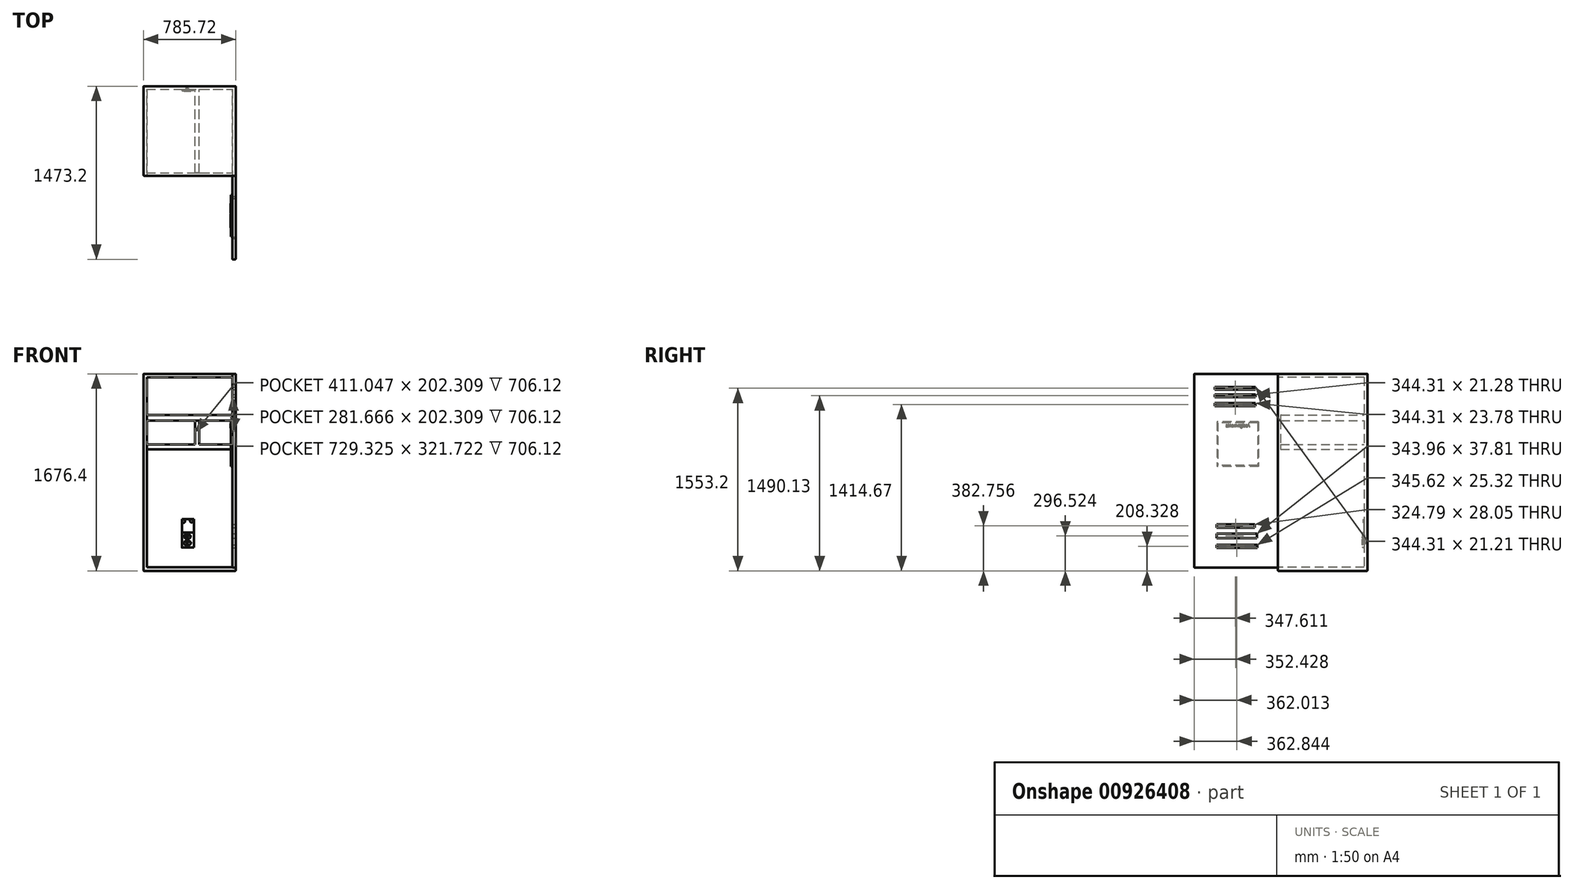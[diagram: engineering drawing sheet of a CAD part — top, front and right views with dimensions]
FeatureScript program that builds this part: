
annotation { "Feature Type Name" : "Feature", "Feature Type Description" : "" }
export const myFeature = defineFeature(function(context is Context, id is Id, definition is map)
    precondition{}
    {
        {
            var Q0;
            Q0=qCreatedBy(makeId("Top.planeOp"),FACE);
            var sketch = newSketch(context, id + "F0", { "sketchPlane" : qUnion([Q0])});
            skLineSegment(sketch, "E0.bottom", {"start": v(-392.86, 381) * mm, "end": v(392.86, 381) * mm});
            skLineSegment(sketch, "E0.top", {"start": v(-392.86, -381) * mm, "end": v(392.86, -381) * mm});
            skLineSegment(sketch, "E0.left", {"start": v(-392.86, 381) * mm, "end": v(-392.86, -381) * mm});
            skLineSegment(sketch, "E0.right", {"start": v(392.86, 381) * mm, "end": v(392.86, -381) * mm});
            skPoint(sketch, "E0.middle", {"position": v(0, 0) * mm});
            skSolve(sketch);
        }
        {
            var Q0;
            Q0=makeQuery(id+"F0.imprint","IMPRINT",FACE,{"disambiguationData":[TD([[makeQuery(id+"F0.imprint","IMPRINT",EDGE,{"derivedFrom":sQuery(id+"F0.wireOp",EDGE,"E0.bottom")}),-1.0]])]});
            extrude(context, id + "F1", {"entities" : qUnion([Q0]), "depth" : 1676.4 * mm, "offsetDistance" : 25.4 * mm});
        }
        {
            var Q0;
            Q0=makeQuery(id+"F1.opExtrude","SWEPT_FACE",FACE,{"disambiguationData":[OSD([sQuery(id+"F0.wireOp",EDGE,"E0.top")])]});
            shell(context, id + "F2", {"entities" : qUnion([Q0]), "thickness" : 28.2 * mm});
        }
        {
            var Q0;
            Q0=makeQuery(id+"F2.opShell","OFFSET_FACE",FACE,{"disambiguationData":[OSD([sQuery(id+"F0.wireOp",EDGE,"E0.bottom")])]});
            var sketch = newSketch(context, id + "F3", { "sketchPlane" : qUnion([Q0])});
            skLineSegment(sketch, "E1.bottom", {"start": v(-66.09, 324.95) * mm, "end": v(35.34, 324.95) * mm});
            skLineSegment(sketch, "E1.top", {"start": v(-66.09, 197.95) * mm, "end": v(35.34, 197.95) * mm});
            skLineSegment(sketch, "E1.left", {"start": v(-66.09, 324.95) * mm, "end": v(-66.09, 197.95) * mm});
            skLineSegment(sketch, "E1.right", {"start": v(35.34, 324.95) * mm, "end": v(35.34, 197.95) * mm});
            skSolve(sketch);
        }
        {
            var Q0;
            Q0=makeQuery(id+"F3.imprint","IMPRINT",FACE,{"disambiguationData":[TD([[makeQuery(id+"F3.imprint","IMPRINT",EDGE,{"derivedFrom":sQuery(id+"F3.wireOp",EDGE,"E1.bottom")}),-1.0]])]});
            extrude(context, id + "F4", {"entities" : qUnion([Q0]), "depth" : 12.7 * mm, "offsetDistance" : 25.4 * mm});
        }
        {
            var Q0;
            Q0=makeQuery(id+"F4.opExtrude","CAP_EDGE",EDGE,{"disambiguationData":[OSD([sQuery(id+"F3.wireOp",EDGE,"E1.left")])],"isStart":true});
            var Q1;
            Q1=makeQuery(id+"F4.opExtrude","CAP_EDGE",EDGE,{"disambiguationData":[OSD([sQuery(id+"F3.wireOp",EDGE,"E1.right")])],"isStart":false});
            var Q2;
            Q2=makeQuery(id+"F4.opExtrude","CAP_EDGE",EDGE,{"disambiguationData":[OSD([sQuery(id+"F3.wireOp",EDGE,"E1.top")])],"isStart":false});
            var Q3;
            Q3=makeQuery(id+"F4.opExtrude","CAP_EDGE",EDGE,{"disambiguationData":[OSD([sQuery(id+"F3.wireOp",EDGE,"E1.bottom")])],"isStart":false});
            fillet(context, id + "F5", {"entities" : qUnion([Q0, Q1, Q2, Q3]), "radius" : 5.08 * mm, "tangentPropagation" : true, "allowEdgeOverflow" : false});
        }
        {
            var Q0;
            Q0=makeQuery(id+"F1.opExtrude","SWEPT_FACE",FACE,{"disambiguationData":[OSD([sQuery(id+"F0.wireOp",EDGE,"E0.top")])]});
            var sketch = newSketch(context, id + "F6", { "sketchPlane" : qUnion([Q0])});
            skLineSegment(sketch, "E2.bottom", {"start": v(392.86, 1676.4) * mm, "end": v(364.66, 1676.4) * mm});
            skLineSegment(sketch, "E2.top", {"start": v(392.86, 28.2) * mm, "end": v(364.66, 28.2) * mm});
            skLineSegment(sketch, "E2.left", {"start": v(392.86, 1676.4) * mm, "end": v(392.86, 28.2) * mm});
            skLineSegment(sketch, "E2.right", {"start": v(364.66, 1676.4) * mm, "end": v(364.66, 28.2) * mm});
            skSolve(sketch);
        }
        {
            var Q0;
            Q0 = qSketchRegion(id + "F6", true);
            extrude(context, id + "F7", {"entities" : qUnion([Q0]), "depth" : 711.2 * mm, "offsetDistance" : 25.4 * mm});
        }
        {
            var Q0;
            Q0=makeQuery(id+"F7.opExtrude","SWEPT_FACE",FACE,{"disambiguationData":[OSD([sQuery(id+"F6.wireOp",EDGE,"E2.left")])]});
            var sketch = newSketch(context, id + "F8", { "sketchPlane" : qUnion([Q0])});
            skLineSegment(sketch, "E3.bottom", {"start": v(-916.74, 1563.8) * mm, "end": v(-572.44, 1563.8) * mm});
            skLineSegment(sketch, "E3.top", {"start": v(-916.74, 1542.6) * mm, "end": v(-572.44, 1542.6) * mm});
            skLineSegment(sketch, "E3.left", {"start": v(-916.74, 1563.8) * mm, "end": v(-916.74, 1542.6) * mm});
            skLineSegment(sketch, "E3.right", {"start": v(-572.44, 1563.8) * mm, "end": v(-572.44, 1542.6) * mm});
            skLineSegment(sketch, "E4.bottom", {"start": v(-916.74, 1500.77) * mm, "end": v(-572.44, 1500.77) * mm});
            skLineSegment(sketch, "E4.top", {"start": v(-916.74, 1479.5) * mm, "end": v(-572.44, 1479.5) * mm});
            skLineSegment(sketch, "E4.left", {"start": v(-916.74, 1500.77) * mm, "end": v(-916.74, 1479.5) * mm});
            skLineSegment(sketch, "E4.right", {"start": v(-572.44, 1500.77) * mm, "end": v(-572.44, 1479.5) * mm});
            skLineSegment(sketch, "E5.bottom", {"start": v(-916.74, 1426.56) * mm, "end": v(-572.44, 1426.56) * mm});
            skLineSegment(sketch, "E5.top", {"start": v(-916.74, 1402.78) * mm, "end": v(-572.44, 1402.78) * mm});
            skLineSegment(sketch, "E5.left", {"start": v(-916.74, 1426.56) * mm, "end": v(-916.74, 1402.78) * mm});
            skLineSegment(sketch, "E5.right", {"start": v(-572.44, 1426.56) * mm, "end": v(-572.44, 1402.78) * mm});
            skLineSegment(sketch, "E6.bottom", {"start": v(-902.17, 315.43) * mm, "end": v(-558.2, 315.43) * mm});
            skLineSegment(sketch, "E6.top", {"start": v(-902.17, 277.62) * mm, "end": v(-558.2, 277.62) * mm});
            skLineSegment(sketch, "E6.left", {"start": v(-902.17, 315.43) * mm, "end": v(-902.17, 277.62) * mm});
            skLineSegment(sketch, "E6.right", {"start": v(-558.2, 315.43) * mm, "end": v(-558.2, 277.62) * mm});
            skLineSegment(sketch, "E7.bottom", {"start": v(-902.17, 220.99) * mm, "end": v(-556.55, 220.99) * mm});
            skLineSegment(sketch, "E7.top", {"start": v(-902.17, 195.67) * mm, "end": v(-556.55, 195.67) * mm});
            skLineSegment(sketch, "E7.left", {"start": v(-902.17, 220.99) * mm, "end": v(-902.17, 195.67) * mm});
            skLineSegment(sketch, "E7.right", {"start": v(-556.55, 220.99) * mm, "end": v(-556.55, 195.67) * mm});
            skLineSegment(sketch, "E8.bottom", {"start": v(-902.17, 396.78) * mm, "end": v(-577.38, 396.78) * mm});
            skLineSegment(sketch, "E8.top", {"start": v(-902.17, 368.73) * mm, "end": v(-577.38, 368.73) * mm});
            skLineSegment(sketch, "E8.left", {"start": v(-902.17, 396.78) * mm, "end": v(-902.17, 368.73) * mm});
            skLineSegment(sketch, "E8.right", {"start": v(-577.38, 396.78) * mm, "end": v(-577.38, 368.73) * mm});
            skSolve(sketch);
        }
        {
            var Q0;
            Q0 = qSketchRegion(id + "F8", true);
            extrude(context, id + "F9", {"entities" : qUnion([Q0]), "operationType" : NewBodyOperationType.REMOVE, "oppositeDirection" : true, "depth" : 1564.64 * mm, "offsetDistance" : 25.4 * mm});
        }
        {
            var Q0;
            Q0=makeQuery(id+"F4.opExtrude","SWEPT_FACE",FACE,{"disambiguationData":[OSD([sQuery(id+"F3.wireOp",EDGE,"E1.bottom")])]});
            var sketch = newSketch(context, id + "F10", { "sketchPlane" : qUnion([Q0])});
            skLineSegment(sketch, "E9.bottom", {"start": v(-66.09, 347.73) * mm, "end": v(35.34, 347.73) * mm});
            skLineSegment(sketch, "E9.top", {"start": v(-66.09, 352.8) * mm, "end": v(35.34, 352.8) * mm});
            skLineSegment(sketch, "E9.left", {"start": v(-66.09, 347.73) * mm, "end": v(-66.09, 352.8) * mm});
            skLineSegment(sketch, "E9.right", {"start": v(35.34, 347.73) * mm, "end": v(35.34, 352.8) * mm});
            skSolve(sketch);
        }
        {
            var Q0;
            Q0 = qSketchRegion(id + "F10", true);
            extrude(context, id + "F11", {"entities" : qUnion([Q0]), "depth" : 116.84 * mm, "offsetDistance" : 25.4 * mm});
        }
        {
            var Q0;
            Q0=makeQuery(id+"F11.opExtrude","SWEPT_FACE",FACE,{"disambiguationData":[OSD([sQuery(id+"F10.wireOp",EDGE,"E9.bottom")])]});
            var sketch = newSketch(context, id + "F12", { "sketchPlane" : qUnion([Q0])});
            skCircle(sketch, "E10", {"center": v(-51.98, 422.55) * mm, "radius": 13.95 * mm});
            skCircle(sketch, "E11", {"center": v(16.54, 425.4) * mm, "radius": 13.24 * mm});
            skSolve(sketch);
        }
        {
            var Q0;
            Q0 = qSketchRegion(id + "F12", true);
            extrude(context, id + "F13", {"entities" : qUnion([Q0]), "operationType" : NewBodyOperationType.ADD, "depth" : 2.54 * mm, "offsetDistance" : 25.4 * mm});
        }
        {
            var Q0;
            Q0=makeQuery(id+"F4.opExtrude","CAP_FACE",FACE,{"disambiguationData":[OSD([sQuery(id+"F3.wireOp",EDGE,"E1.bottom"),sQuery(id+"F3.wireOp",EDGE,"E1.top"),sQuery(id+"F3.wireOp",EDGE,"E1.left"),sQuery(id+"F3.wireOp",EDGE,"E1.right")])],"isStart":false});
            var sketch = newSketch(context, id + "F14", { "sketchPlane" : qUnion([Q0])});
            skArc(sketch, "E12", {"start": v(-39.05, 307.45) * mm, "mid": v(-46.6, 290.51) * mm, "end": v(-34.67, 276.31) * mm});
            skLineSegment(sketch, "E13", {"start": v(-39.05, 307.45) * mm, "end": v(0, 307.45) * mm});
            skLineSegment(sketch, "E14", {"start": v(-34.67, 276.31) * mm, "end": v(0, 276.31) * mm});
            skArc(sketch, "E15", {"start": v(0, 276.31) * mm, "mid": v(8.82, 291.88) * mm, "end": v(0, 307.45) * mm});
            skSolve(sketch);
        }
        {
            var Q0;
            Q0=makeQuery(id+"F14.imprint","IMPRINT",FACE,{"disambiguationData":[TD([[makeQuery(id+"F14.imprint","IMPRINT",EDGE,{"derivedFrom":sQuery(id+"F14.wireOp",EDGE,"E12")}),1.0]])]});
            extrude(context, id + "F15", {"entities" : qUnion([Q0]), "operationType" : NewBodyOperationType.ADD, "depth" : 2.54 * mm, "offsetDistance" : 25.4 * mm});
        }
        {
            var Q0;
            Q0=makeQuery(id+"F15.opExtrude","CAP_FACE",FACE,{"disambiguationData":[OSD([sQuery(id+"F14.wireOp",EDGE,"E12"),sQuery(id+"F14.wireOp",EDGE,"E13"),sQuery(id+"F14.wireOp",EDGE,"E14"),sQuery(id+"F14.wireOp",EDGE,"E15")])],"isStart":false});
            var sketch = newSketch(context, id + "F16", { "sketchPlane" : qUnion([Q0])});
            skLineSegment(sketch, "E16.bottom", {"start": v(-31.97, 304.65) * mm, "end": v(-29.27, 304.65) * mm});
            skLineSegment(sketch, "E16.top", {"start": v(-31.97, 292.95) * mm, "end": v(-29.27, 292.95) * mm});
            skLineSegment(sketch, "E16.left", {"start": v(-31.97, 304.65) * mm, "end": v(-31.97, 292.95) * mm});
            skLineSegment(sketch, "E16.right", {"start": v(-29.27, 304.65) * mm, "end": v(-29.27, 292.95) * mm});
            skLineSegment(sketch, "E17.bottom", {"start": v(-11.77, 305.88) * mm, "end": v(-9.34, 305.88) * mm});
            skLineSegment(sketch, "E17.top", {"start": v(-11.77, 291.88) * mm, "end": v(-9.34, 291.88) * mm});
            skLineSegment(sketch, "E17.left", {"start": v(-11.77, 305.88) * mm, "end": v(-11.77, 291.88) * mm});
            skLineSegment(sketch, "E17.right", {"start": v(-9.34, 305.88) * mm, "end": v(-9.34, 291.88) * mm});
            skArc(sketch, "E18", {"start": v(-12, 281.24) * mm, "mid": v(-19.6, 287.03) * mm, "end": v(-27.21, 281.25) * mm});
            skLineSegment(sketch, "E19", {"start": v(-27.21, 281.25) * mm, "end": v(-12, 281.24) * mm});
            skSolve(sketch);
        }
        {
            var Q0;
            Q0=makeQuery(id+"F16.imprint","IMPRINT",FACE,{"disambiguationData":[TD([[makeQuery(id+"F16.imprint","IMPRINT",EDGE,{"derivedFrom":sQuery(id+"F16.wireOp",EDGE,"E16.bottom")}),-1.0]])]});
            var Q1;
            Q1=makeQuery(id+"F16.imprint","IMPRINT",FACE,{"disambiguationData":[TD([[makeQuery(id+"F16.imprint","IMPRINT",EDGE,{"derivedFrom":sQuery(id+"F16.wireOp",EDGE,"E17.bottom")}),-1.0]])]});
            var Q2;
            Q2=makeQuery(id+"F16.imprint","IMPRINT",FACE,{"disambiguationData":[TD([[makeQuery(id+"F16.imprint","IMPRINT",EDGE,{"derivedFrom":sQuery(id+"F16.wireOp",EDGE,"E18")}),1.0]])]});
            extrude(context, id + "F17", {"entities" : qUnion([Q0, Q1, Q2]), "operationType" : NewBodyOperationType.REMOVE, "oppositeDirection" : true, "depth" : 17.02 * mm, "offsetDistance" : 25.4 * mm});
        }
        {
            var Q0;
            Q0=makeQuery(id+"F4.opExtrude","CAP_FACE",FACE,{"disambiguationData":[OSD([sQuery(id+"F3.wireOp",EDGE,"E1.bottom"),sQuery(id+"F3.wireOp",EDGE,"E1.top"),sQuery(id+"F3.wireOp",EDGE,"E1.left"),sQuery(id+"F3.wireOp",EDGE,"E1.right")])],"isStart":false});
            var sketch = newSketch(context, id + "F18", { "sketchPlane" : qUnion([Q0])});
            skArc(sketch, "E20", {"start": v(-35.8, 252.29) * mm, "mid": v(-48.73, 238.08) * mm, "end": v(-38.63, 221.73) * mm});
            skLineSegment(sketch, "E21", {"start": v(-38.63, 221.73) * mm, "end": v(0, 221.73) * mm});
            skArc(sketch, "E22", {"start": v(0, 221.73) * mm, "mid": v(10.82, 237.33) * mm, "end": v(0, 252.94) * mm});
            skLineSegment(sketch, "E23", {"start": v(-35.8, 252.29) * mm, "end": v(0, 252.94) * mm});
            skSolve(sketch);
        }
        {
            var Q0;
            Q0=makeQuery(id+"F18.imprint","IMPRINT",FACE,{"disambiguationData":[TD([[makeQuery(id+"F18.imprint","IMPRINT",EDGE,{"derivedFrom":sQuery(id+"F18.wireOp",EDGE,"E20")}),1.0]])]});
            extrude(context, id + "F19", {"entities" : qUnion([Q0]), "operationType" : NewBodyOperationType.ADD, "depth" : 2.54 * mm, "offsetDistance" : 25.4 * mm});
        }
        {
            var Q0;
            Q0=makeQuery(id+"F4.opExtrude","CAP_FACE",FACE,{"disambiguationData":[OSD([sQuery(id+"F3.wireOp",EDGE,"E1.bottom"),sQuery(id+"F3.wireOp",EDGE,"E1.top"),sQuery(id+"F3.wireOp",EDGE,"E1.left"),sQuery(id+"F3.wireOp",EDGE,"E1.right")])],"isStart":false});
            var sketch = newSketch(context, id + "F20", { "sketchPlane" : qUnion([Q0])});
            skCircle(sketch, "E24", {"center": v(-19.94, 262.87) * mm, "radius": 6.46 * mm});
            skSolve(sketch);
        }
        {
            var Q0;
            Q0=makeQuery(id+"F20.imprint","IMPRINT",FACE,{"disambiguationData":[TD([[makeQuery(id+"F20.imprint","IMPRINT",EDGE,{"derivedFrom":sQuery(id+"F20.wireOp",EDGE,"E24")}),1.0]])]});
            extrude(context, id + "F21", {"entities" : qUnion([Q0]), "operationType" : NewBodyOperationType.ADD, "depth" : 2.54 * mm, "offsetDistance" : 25.4 * mm});
        }
        {
            var Q0;
            Q0=makeQuery(id+"F21.opExtrude","CAP_FACE",FACE,{"disambiguationData":[OSD([sQuery(id+"F20.wireOp",EDGE,"E24")])],"isStart":false});
            var sketch = newSketch(context, id + "F22", { "sketchPlane" : qUnion([Q0])});
            skLineSegment(sketch, "E25.bottom", {"start": v(-20.92, 268.23) * mm, "end": v(-19, 268.23) * mm});
            skLineSegment(sketch, "E25.top", {"start": v(-20.92, 257.7) * mm, "end": v(-19, 257.7) * mm});
            skLineSegment(sketch, "E25.left", {"start": v(-20.92, 268.23) * mm, "end": v(-20.92, 257.7) * mm});
            skLineSegment(sketch, "E25.right", {"start": v(-19, 268.23) * mm, "end": v(-19, 257.7) * mm});
            skSolve(sketch);
        }
        {
            var Q0;
            Q0 = qSketchRegion(id + "F22", true);
            extrude(context, id + "F23", {"entities" : qUnion([Q0]), "operationType" : NewBodyOperationType.REMOVE, "oppositeDirection" : true, "depth" : 25.4 * mm, "offsetDistance" : 25.4 * mm});
        }
        {
            var Q0;
            Q0=makeQuery(id+"F19.opExtrude","CAP_FACE",FACE,{"disambiguationData":[OSD([sQuery(id+"F18.wireOp",EDGE,"E20"),sQuery(id+"F18.wireOp",EDGE,"E21"),sQuery(id+"F18.wireOp",EDGE,"E22"),sQuery(id+"F18.wireOp",EDGE,"E23")])],"isStart":false});
            var sketch = newSketch(context, id + "F24", { "sketchPlane" : qUnion([Q0])});
            skLineSegment(sketch, "E26.bottom", {"start": v(-32.72, 248.41) * mm, "end": v(-29.82, 248.41) * mm});
            skLineSegment(sketch, "E26.top", {"start": v(-32.72, 237.1) * mm, "end": v(-29.82, 237.1) * mm});
            skLineSegment(sketch, "E26.left", {"start": v(-32.72, 248.41) * mm, "end": v(-32.72, 237.1) * mm});
            skLineSegment(sketch, "E26.right", {"start": v(-29.82, 248.41) * mm, "end": v(-29.82, 237.1) * mm});
            skLineSegment(sketch, "E27.bottom", {"start": v(-14.05, 248.73) * mm, "end": v(-10.86, 248.73) * mm});
            skLineSegment(sketch, "E27.top", {"start": v(-14.05, 237.1) * mm, "end": v(-10.86, 237.1) * mm});
            skLineSegment(sketch, "E27.left", {"start": v(-14.05, 248.73) * mm, "end": v(-14.05, 237.1) * mm});
            skLineSegment(sketch, "E27.right", {"start": v(-10.86, 248.73) * mm, "end": v(-10.86, 237.1) * mm});
            skArc(sketch, "E28", {"start": v(-15.66, 226.82) * mm, "mid": v(-21.05, 232.9) * mm, "end": v(-27.13, 227.51) * mm});
            skLineSegment(sketch, "E29", {"start": v(-27.13, 227.51) * mm, "end": v(-15.66, 226.82) * mm});
            skSolve(sketch);
        }
        {
            var Q0;
            Q0 = qSketchRegion(id + "F24", true);
            extrude(context, id + "F25", {"entities" : qUnion([Q0]), "operationType" : NewBodyOperationType.REMOVE, "oppositeDirection" : true, "depth" : 25.4 * mm, "offsetDistance" : 25.4 * mm});
        }
        {
            var Q0;
            Q0=makeQuery(id+"F2.opShell","OFFSET_FACE",FACE,{"disambiguationData":[OSD([sQuery(id+"F0.wireOp",EDGE,"E0.bottom")])]});
            var sketch = newSketch(context, id + "F26", { "sketchPlane" : qUnion([Q0])});
            skLineSegment(sketch, "E30.bottom", {"start": v(-364.66, 1326.48) * mm, "end": v(364.66, 1326.48) * mm});
            skLineSegment(sketch, "E30.top", {"start": v(-364.66, 1279.01) * mm, "end": v(364.66, 1279.01) * mm});
            skLineSegment(sketch, "E30.left", {"start": v(-364.66, 1326.48) * mm, "end": v(-364.66, 1279.01) * mm});
            skLineSegment(sketch, "E30.right", {"start": v(364.66, 1326.48) * mm, "end": v(364.66, 1279.01) * mm});
            skSolve(sketch);
        }
        {
            var Q0;
            Q0 = qSketchRegion(id + "F26", true);
            extrude(context, id + "F27", {"entities" : qUnion([Q0]), "operationType" : NewBodyOperationType.ADD, "depth" : 711.2 * mm, "offsetDistance" : 25.4 * mm});
        }
        {
            var Q0;
            Q0=makeQuery(id+"F27.opExtrude","CAP_EDGE",EDGE,{"disambiguationData":[OSD([sQuery(id+"F26.wireOp",EDGE,"E30.bottom")])],"isStart":false});
            var Q1;
            Q1=makeQuery(id+"F27.opExtrude","CAP_EDGE",EDGE,{"disambiguationData":[OSD([sQuery(id+"F26.wireOp",EDGE,"E30.top")])],"isStart":false});
            var Q2;
            Q2=makeQuery(id+"F11.opExtrude","CAP_EDGE",EDGE,{"disambiguationData":[OSD([sQuery(id+"F10.wireOp",EDGE,"E9.bottom")])],"isStart":false});
            var Q3;
            Q3=makeQuery(id+"F11.opExtrude","SWEPT_EDGE",EDGE,{"disambiguationData":[OSD([sQuery(id+"F3.wireOp",EDGE,"E1.bottom"),sQuery(id+"F3.wireOp",EDGE,"E1.left"),sQuery(id+"F10.wireOp",EDGE,"E9.bottom"),sQuery(id+"F10.wireOp",EDGE,"E9.left")])]});
            var Q4;
            Q4=makeQuery(id+"F11.opExtrude","SWEPT_EDGE",EDGE,{"disambiguationData":[OSD([sQuery(id+"F3.wireOp",EDGE,"E1.bottom"),sQuery(id+"F3.wireOp",EDGE,"E1.right"),sQuery(id+"F10.wireOp",EDGE,"E9.bottom"),sQuery(id+"F10.wireOp",EDGE,"E9.right")])]});
            fillet(context, id + "F28", {"entities" : qUnion([Q0, Q1, Q2, Q3, Q4]), "radius" : 5.08 * mm, "tangentPropagation" : true, "allowEdgeOverflow" : false});
        }
        {
            var Q0;
            Q0=makeQuery(id+"F7.opExtrude","SWEPT_FACE",FACE,{"disambiguationData":[OSD([sQuery(id+"F6.wireOp",EDGE,"E2.right")])]});
            var sketch = newSketch(context, id + "F29", { "sketchPlane" : qUnion([Q0])});
            skLineSegment(sketch, "E31.bottom", {"start": v(545.05, 1268.4) * mm, "end": v(898.86, 1268.4) * mm});
            skLineSegment(sketch, "E31.top", {"start": v(545.05, 888.9) * mm, "end": v(898.86, 888.9) * mm});
            skLineSegment(sketch, "E31.left", {"start": v(545.05, 1268.4) * mm, "end": v(545.05, 888.9) * mm});
            skLineSegment(sketch, "E31.right", {"start": v(898.86, 1268.4) * mm, "end": v(898.86, 888.9) * mm});
            skSolve(sketch);
        }
        {
            var Q0;
            Q0 = qSketchRegion(id + "F29", true);
            extrude(context, id + "F30", {"entities" : qUnion([Q0]), "depth" : 12.7 * mm, "offsetDistance" : 25.4 * mm});
        }
        {
            var Q0;
            Q0=makeQuery(id+"F30.opExtrude","CAP_FACE",FACE,{"disambiguationData":[OSD([sQuery(id+"F29.wireOp",EDGE,"E31.bottom"),sQuery(id+"F29.wireOp",EDGE,"E31.top"),sQuery(id+"F29.wireOp",EDGE,"E31.left"),sQuery(id+"F29.wireOp",EDGE,"E31.right")])],"isStart":false});
            shell(context, id + "F31", {"entities" : qUnion([Q0]), "thickness" : 7.62 * mm});
        }
        {
            var Q0;
            Q0=makeQuery(id+"F31.opShell","OFFSET_FACE",FACE,{"disambiguationData":[OSD([sQuery(id+"F29.wireOp",EDGE,"E31.bottom"),sQuery(id+"F29.wireOp",EDGE,"E31.top"),sQuery(id+"F29.wireOp",EDGE,"E31.left"),sQuery(id+"F29.wireOp",EDGE,"E31.right")])]});
            var sketch = newSketch(context, id + "F32", { "sketchPlane" : qUnion([Q0])});
            skText(sketch, "E32", { "text": "Assignments", "fontName": "OpenSans-Regular.ttf"});
            const initialGuessF32  = {"E32": [0.61883, 1.2247, 1, 0, 0.02498]};
            skSetInitialGuess(sketch, initialGuessF32);
            skSolve(sketch);
        }
        {
            var Q0;
            Q0 = qSketchRegion(id + "F32", true);
            extrude(context, id + "F33", {"entities" : qUnion([Q0]), "operationType" : NewBodyOperationType.ADD, "depth" : 10.16 * mm, "offsetDistance" : 25.4 * mm});
        }
        {
            var Q0;
            Q0=makeQuery(id+"F1.opExtrude","SWEPT_EDGE",EDGE,{"disambiguationData":[OSD([sQuery(id+"F0.wireOp",EDGE,"E0.bottom"),sQuery(id+"F0.wireOp",EDGE,"E0.right")])]});
            var Q1;
            Q1=makeQuery(id+"F1.opExtrude","SWEPT_EDGE",EDGE,{"disambiguationData":[OSD([sQuery(id+"F0.wireOp",EDGE,"E0.bottom"),sQuery(id+"F0.wireOp",EDGE,"E0.left")])]});
            var Q2;
            Q2=makeQuery(id+"F1.opExtrude","CAP_EDGE",EDGE,{"disambiguationData":[OSD([sQuery(id+"F0.wireOp",EDGE,"E0.right")])],"isStart":false});
            var Q3;
            Q3=makeQuery(id+"F1.opExtrude","CAP_EDGE",EDGE,{"disambiguationData":[OSD([sQuery(id+"F0.wireOp",EDGE,"E0.left")])],"isStart":false});
            var Q4;
            Q4=makeQuery(id+"F1.opExtrude","SWEPT_EDGE",EDGE,{"disambiguationData":[OSD([sQuery(id+"F0.wireOp",EDGE,"E0.top"),sQuery(id+"F0.wireOp",EDGE,"E0.left")])]});
            var Q5;
            Q5=makeQuery(id+"F7.opExtrude","CAP_EDGE",EDGE,{"disambiguationData":[OSD([sQuery(id+"F6.wireOp",EDGE,"E2.left")])],"isStart":true});
            var Q6;
            Q6=makeQuery(id+"F7.opExtrude","SWEPT_EDGE",EDGE,{"disambiguationData":[OSD([sQuery(id+"F0.wireOp",EDGE,"E0.top"),sQuery(id+"F6.wireOp",EDGE,"E2.bottom"),sQuery(id+"F6.wireOp",EDGE,"E2.right")])]});
            var Q7;
            Q7=makeQuery(id+"F7.opExtrude","SWEPT_EDGE",EDGE,{"disambiguationData":[OSD([sQuery(id+"F6.wireOp",EDGE,"E2.bottom"),sQuery(id+"F6.wireOp",EDGE,"E2.left")])]});
            var Q8;
            Q8=makeQuery(id+"F7.opExtrude","CAP_EDGE",EDGE,{"disambiguationData":[OSD([sQuery(id+"F6.wireOp",EDGE,"E2.left")])],"isStart":false});
            var Q9;
            Q9=makeQuery(id+"F7.opExtrude","SWEPT_EDGE",EDGE,{"disambiguationData":[OSD([sQuery(id+"F0.wireOp",EDGE,"E0.top"),sQuery(id+"F6.wireOp",EDGE,"E2.top"),sQuery(id+"F6.wireOp",EDGE,"E2.right")])]});
            var Q10;
            Q10=makeQuery(id+"F1.opExtrude","CAP_EDGE",EDGE,{"disambiguationData":[OSD([sQuery(id+"F0.wireOp",EDGE,"E0.top")])],"isStart":true});
            var Q11;
            Q11=makeQuery(id+"F1.opExtrude","CAP_EDGE",EDGE,{"disambiguationData":[OSD([sQuery(id+"F0.wireOp",EDGE,"E0.right")])],"isStart":true});
            var Q12;
            Q12=makeQuery(id+"F1.opExtrude","CAP_EDGE",EDGE,{"disambiguationData":[OSD([sQuery(id+"F0.wireOp",EDGE,"E0.left")])],"isStart":true});
            var Q13;
            Q13=makeQuery(id+"F1.opExtrude","CAP_EDGE",EDGE,{"disambiguationData":[OSD([sQuery(id+"F0.wireOp",EDGE,"E0.bottom")])],"isStart":true});
            fillet(context, id + "F34", {"entities" : qUnion([Q0, Q1, Q2, Q3, Q4, Q5, Q6, Q7, Q8, Q9, Q10, Q11, Q12, Q13]), "radius" : 5.08 * mm, "tangentPropagation" : true, "allowEdgeOverflow" : false});
        }
        {
            var Q0;
            {var subQ0=sQuery(id+"F0.wireOp",EDGE,"E0.right");var subQ1=sQuery(id+"F0.wireOp",EDGE,"E0.left");var subQ2=sQuery(id+"F0.wireOp",EDGE,"E0.top");var subQ3=sQuery(id+"F0.wireOp",EDGE,"E0.bottom");Q0=makeQuery(id+"F2.opShell","OFFSET_FACE",FACE,{"disambiguationData":[OSD([subQ3,subQ2,subQ1,subQ0]),TDD([makeQuery(id+"F1.opExtrude","CAP_FACE",FACE,{"disambiguationData":[OSD([subQ3,subQ2,subQ1,subQ0])],"isStart":true})])]});}
            var sketch = newSketch(context, id + "F35", { "sketchPlane" : qUnion([Q0])});
            skLineSegment(sketch, "E33.bottom", {"start": v(-364.66, 352.8) * mm, "end": v(364.66, 352.8) * mm});
            skLineSegment(sketch, "E33.top", {"start": v(-364.66, -381) * mm, "end": v(364.66, -381) * mm});
            skLineSegment(sketch, "E33.left", {"start": v(-364.66, 352.8) * mm, "end": v(-364.66, -381) * mm});
            skLineSegment(sketch, "E33.right", {"start": v(364.66, 352.8) * mm, "end": v(364.66, -381) * mm});
            skSolve(sketch);
        }
        {
            var Q0;
            Q0 = qSketchRegion(id + "F35", true);
            extrude(context, id + "F36", {"entities" : qUnion([Q0]), "operationType" : NewBodyOperationType.ADD, "depth" : 2.54 * mm, "offsetDistance" : 25.4 * mm});
        }
        {
            var Q0;
            {var subQ3=sQuery(id+"F0.wireOp",EDGE,"E0.bottom");Q0=makeQuery(id+"F27.boolean.opBoolean","SPLIT",FACE,{"disambiguationData":[TD([makeQuery(id+"F27.opExtrude","SWEPT_FACE",FACE,{"disambiguationData":[OSD([sQuery(id+"F26.wireOp",EDGE,"E30.top")])]})])],"derivedFrom":makeQuery(id+"F2.opShell","OFFSET_FACE",FACE,{"disambiguationData":[OSD([subQ3])]})});}
            var sketch = newSketch(context, id + "F37", { "sketchPlane" : qUnion([Q0])});
            skLineSegment(sketch, "E34.bottom", {"start": v(-364.66, 1076.7) * mm, "end": v(364.66, 1076.7) * mm});
            skLineSegment(sketch, "E34.top", {"start": v(-364.66, 1034.98) * mm, "end": v(364.66, 1034.98) * mm});
            skLineSegment(sketch, "E34.left", {"start": v(-364.66, 1076.7) * mm, "end": v(-364.66, 1034.98) * mm});
            skLineSegment(sketch, "E34.right", {"start": v(364.66, 1076.7) * mm, "end": v(364.66, 1034.98) * mm});
            skSolve(sketch);
        }
        {
            var Q0;
            Q0=makeQuery(id+"F37.imprint","IMPRINT",FACE,{"disambiguationData":[TD([[makeQuery(id+"F37.imprint","IMPRINT",EDGE,{"derivedFrom":sQuery(id+"F37.wireOp",EDGE,"E34.bottom")}),-1.0]])]});
            extrude(context, id + "F38", {"entities" : qUnion([Q0]), "operationType" : NewBodyOperationType.ADD, "depth" : 711.2 * mm, "offsetDistance" : 25.4 * mm});
        }
        {
            var Q0;
            {var subQ2=makeQuery(id+"F27.opExtrude","SWEPT_FACE",FACE,{"disambiguationData":[OSD([sQuery(id+"F26.wireOp",EDGE,"E30.top")])]});var subQ6=sQuery(id+"F0.wireOp",EDGE,"E0.bottom");Q0=makeQuery(id+"F38.boolean.opBoolean","SPLIT",FACE,{"disambiguationData":[TD([subQ2])],"derivedFrom":makeQuery(id+"F27.boolean.opBoolean","SPLIT",FACE,{"disambiguationData":[TD([subQ2])],"derivedFrom":makeQuery(id+"F2.opShell","OFFSET_FACE",FACE,{"disambiguationData":[OSD([subQ6])]})})});}
            var sketch = newSketch(context, id + "F39", { "sketchPlane" : qUnion([Q0])});
            skLineSegment(sketch, "E35.bottom", {"start": v(46.38, 1279.01) * mm, "end": v(83, 1279.01) * mm});
            skLineSegment(sketch, "E35.top", {"start": v(46.38, 1076.7) * mm, "end": v(83, 1076.7) * mm});
            skLineSegment(sketch, "E35.left", {"start": v(46.38, 1279.01) * mm, "end": v(46.38, 1076.7) * mm});
            skLineSegment(sketch, "E35.right", {"start": v(83, 1279.01) * mm, "end": v(83, 1076.7) * mm});
            skSolve(sketch);
        }
        {
            var Q0;
            Q0 = qSketchRegion(id + "F39", true);
            extrude(context, id + "F40", {"entities" : qUnion([Q0]), "operationType" : NewBodyOperationType.ADD, "depth" : 711.2 * mm, "offsetDistance" : 25.4 * mm});
        }
    });
